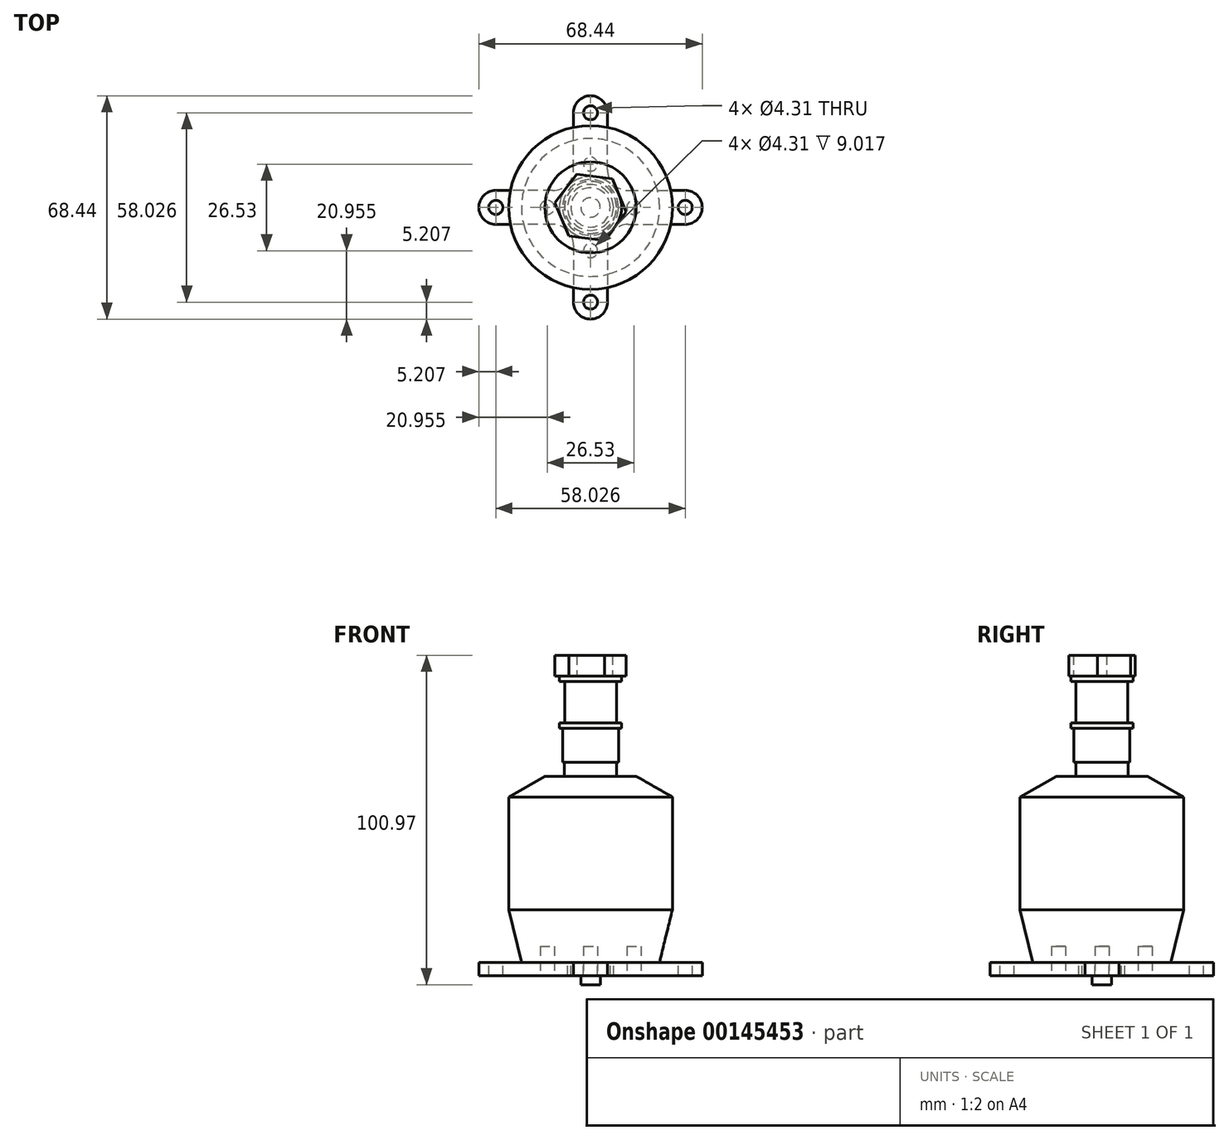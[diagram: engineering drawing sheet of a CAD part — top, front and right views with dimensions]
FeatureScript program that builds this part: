
annotation { "Feature Type Name" : "Feature", "Feature Type Description" : "" }
export const myFeature = defineFeature(function(context is Context, id is Id, definition is map)
    precondition{}
    {
        {
            var Q0;
            Q0=qCreatedBy(makeId("Top.planeOp"),FACE);
            var sketch = newSketch(context, id + "F0", { "sketchPlane" : qUnion([Q0])});
            skCircle(sketch, "E0", {"center": v(0, 0) * mm, "radius": 21.15 * mm});
            skSolve(sketch);
        }
        {
            var Q0;
            Q0=qCreatedBy(makeId("Top.planeOp"),FACE);
            cPlane(context, id + "F1", {"entities" : qUnion([Q0]), "cplaneType" : CPlaneType.OFFSET, "offset" : 16.13 * mm, "width" : 152.4 * mm, "height" : 152.4 * mm});
        }
        {
            var Q0;
            Q0=qCreatedBy(id+"F1.planeOp",FACE);
            var sketch = newSketch(context, id + "F2", { "sketchPlane" : qUnion([Q0])});
            skCircle(sketch, "E1", {"center": v(0, 0) * mm, "radius": 25.08 * mm});
            skSolve(sketch);
        }
        {
            var Q0;
            Q0=makeQuery(id+"F0.imprint","IMPRINT",FACE,{"disambiguationData":[TD([[makeQuery(id+"F0.imprint","IMPRINT",EDGE,{"derivedFrom":sQuery(id+"F0.wireOp",EDGE,"E0")}),1.0]])]});
            var Q1;
            Q1=makeQuery(id+"F2.imprint","IMPRINT",FACE,{"disambiguationData":[TD([[makeQuery(id+"F2.imprint","IMPRINT",EDGE,{"derivedFrom":sQuery(id+"F2.wireOp",EDGE,"E1")}),1.0]])]});
            loft(context, id + "F3", {"sheetProfilesArray" : [{ "sheetProfileEntities" : qUnion([Q0]) }, { "sheetProfileEntities" : qUnion([Q1]) }]});
        }
        {
            var Q0;
            Q0=makeQuery(id+"F3.opLoft","CAP_FACE",FACE,{"disambiguationData":[OSD([makeQuery(id+"F2.imprint","IMPRINT",FACE,{"disambiguationData":[TD([[makeQuery(id+"F2.imprint","IMPRINT",EDGE,{"derivedFrom":sQuery(id+"F2.wireOp",EDGE,"E1")}),1.0]])]})])],"isStart":true});
            extrude(context, id + "F4", {"entities" : qUnion([Q0]), "depth" : 34.54 * mm});
        }
        {
            var Q0;
            Q0=makeQuery(id+"F4.opExtrude","CAP_FACE",FACE,{"disambiguationData":[OSD([makeQuery(id+"F2.imprint","IMPRINT",FACE,{"disambiguationData":[TD([[makeQuery(id+"F2.imprint","IMPRINT",EDGE,{"derivedFrom":sQuery(id+"F2.wireOp",EDGE,"E1")}),1.0]])]})])],"isStart":false});
            cPlane(context, id + "F5", {"entities" : qUnion([Q0]), "cplaneType" : CPlaneType.OFFSET, "offset" : 6.35 * mm, "width" : 152.4 * mm, "height" : 152.4 * mm});
        }
        {
            var Q0;
            Q0=qCreatedBy(id+"F5.planeOp",FACE);
            var sketch = newSketch(context, id + "F6", { "sketchPlane" : qUnion([Q0])});
            skCircle(sketch, "E2", {"center": v(0, 0) * mm, "radius": 13.97 * mm});
            skSolve(sketch);
        }
        {
            var Q1;
            Q1=makeQuery(id+"F6.imprint","IMPRINT",FACE,{"disambiguationData":[TD([[makeQuery(id+"F6.imprint","IMPRINT",EDGE,{"derivedFrom":sQuery(id+"F6.wireOp",EDGE,"E2")}),1.0]])]});
            var Q2;
            Q2=makeQuery(id+"F4.opExtrude","CAP_FACE",FACE,{"disambiguationData":[OSD([makeQuery(id+"F2.imprint","IMPRINT",FACE,{"disambiguationData":[TD([[makeQuery(id+"F2.imprint","IMPRINT",EDGE,{"derivedFrom":sQuery(id+"F2.wireOp",EDGE,"E1")}),1.0]])]})])],"isStart":false});
            loft(context, id + "F7", {"operationType" : NewBodyOperationType.ADD, "sheetProfilesArray" : [{ "sheetProfileEntities" : qUnion([Q1]) }, { "sheetProfileEntities" : qUnion([Q2]) }]});
        }
        {
            var Q0;
            Q0=makeQuery(id+"F7.opLoft","CAP_FACE",FACE,{"disambiguationData":[OSD([makeQuery(id+"F6.imprint","IMPRINT",FACE,{"disambiguationData":[TD([[makeQuery(id+"F6.imprint","IMPRINT",EDGE,{"derivedFrom":sQuery(id+"F6.wireOp",EDGE,"E2")}),1.0]])]})])],"isStart":true});
            var sketch = newSketch(context, id + "F8", { "sketchPlane" : qUnion([Q0])});
            skCircle(sketch, "E3", {"center": v(0, 0) * mm, "radius": 8 * mm});
            skSolve(sketch);
        }
        {
            var Q0;
            Q0 = qSketchRegion(id + "F8", true);
            extrude(context, id + "F9", {"entities" : qUnion([Q0]), "operationType" : NewBodyOperationType.ADD, "depth" : 4.32 * mm});
        }
        {
            var Q0;
            Q0=makeQuery(id+"F9.opExtrude","CAP_FACE",FACE,{"disambiguationData":[OSD([sQuery(id+"F8.wireOp",EDGE,"E3")])],"isStart":false});
            var sketch = newSketch(context, id + "F10", { "sketchPlane" : qUnion([Q0])});
            skCircle(sketch, "E4", {"center": v(0, 0) * mm, "radius": 3 * mm});
            skSolve(sketch);
        }
        {
            var Q0;
            Q0 = qSketchRegion(id + "F10", true);
            extrude(context, id + "F11", {"entities" : qUnion([Q0]), "operationType" : NewBodyOperationType.ADD, "depth" : 15.24 * mm});
        }
        {
            var Q0;
            Q0=makeQuery(id+"F3.opLoft","CAP_FACE",FACE,{"disambiguationData":[OSD([makeQuery(id+"F0.imprint","IMPRINT",FACE,{"disambiguationData":[TD([[makeQuery(id+"F0.imprint","IMPRINT",EDGE,{"derivedFrom":sQuery(id+"F0.wireOp",EDGE,"E0")}),1.0]])]})])],"isStart":true});
            var sketch = newSketch(context, id + "F12", { "sketchPlane" : qUnion([Q0])});
            skCircle(sketch, "E5", {"center": v(0, 0) * mm, "radius": 6.03 * mm});
            skSolve(sketch);
        }
        {
            var Q0;
            Q0 = qSketchRegion(id + "F12", true);
            extrude(context, id + "F13", {"entities" : qUnion([Q0]), "operationType" : NewBodyOperationType.ADD, "depth" : 4.06 * mm});
        }
        {
            var Q0;
            Q0=makeQuery(id+"F13.opExtrude","CAP_FACE",FACE,{"disambiguationData":[OSD([sQuery(id+"F12.wireOp",EDGE,"E5")])],"isStart":false});
            var sketch = newSketch(context, id + "F14", { "sketchPlane" : qUnion([Q0])});
            skCircle(sketch, "E6", {"center": v(0, 0) * mm, "radius": 2.98 * mm});
            skSolve(sketch);
        }
        {
            var Q0;
            Q0 = qSketchRegion(id + "F14", true);
            extrude(context, id + "F15", {"entities" : qUnion([Q0]), "operationType" : NewBodyOperationType.ADD, "depth" : 2.8 * mm});
        }
        {
            var Q0;
            Q0=makeQuery(id+"F3.opLoft","CAP_FACE",FACE,{"disambiguationData":[OSD([makeQuery(id+"F0.imprint","IMPRINT",FACE,{"disambiguationData":[TD([[makeQuery(id+"F0.imprint","IMPRINT",EDGE,{"derivedFrom":sQuery(id+"F0.wireOp",EDGE,"E0")}),1.0]])]})])],"isStart":true});
            var sketch = newSketch(context, id + "F16", { "sketchPlane" : qUnion([Q0])});
            skCircle(sketch, "E7", {"center": v(0, 13.27) * mm, "radius": 2.15 * mm});
            skCircle(sketch, "E8", {"center": v(13.27, 0) * mm, "radius": 2.15 * mm});
            skCircle(sketch, "E9", {"center": v(0, -13.27) * mm, "radius": 2.15 * mm});
            skCircle(sketch, "E10", {"center": v(-13.27, 0) * mm, "radius": 2.15 * mm});
            skCircle(sketch, "E11", {"center": v(0, 0) * mm, "radius": 11.11 * mm, "construction": true});
            skSolve(sketch);
        }
        {
            var Q0;
            Q0 = qSketchRegion(id + "F16", true);
            extrude(context, id + "F17", {"entities" : qUnion([Q0]), "operationType" : NewBodyOperationType.REMOVE, "oppositeDirection" : true, "depth" : 4.95 * mm});
        }
        {
            var Q0;
            Q0=makeQuery(id+"F3.opLoft","CAP_FACE",FACE,{"disambiguationData":[OSD([makeQuery(id+"F0.imprint","IMPRINT",FACE,{"disambiguationData":[TD([[makeQuery(id+"F0.imprint","IMPRINT",EDGE,{"derivedFrom":sQuery(id+"F0.wireOp",EDGE,"E0")}),1.0]])]})])],"isStart":true});
            var sketch = newSketch(context, id + "F18", { "sketchPlane" : qUnion([Q0])});
            skCircle(sketch, "E12", {"center": v(0, 0) * mm, "radius": 7.05 * mm});
            skLineSegment(sketch, "E13.left", {"start": v(5.2, 11.56) * mm, "end": v(5.2, 29.01) * mm});
            skLineSegment(sketch, "E13.right", {"start": v(-5.2, 11.56) * mm, "end": v(-5.2, 29.01) * mm});
            skPoint(sketch, "E13.middle", {"position": v(0, 18.28) * mm});
            skLineSegment(sketch, "E14", {"start": v(-5.2, 29.01) * mm, "end": v(5.2, 29.01) * mm, "construction": true});
            skArc(sketch, "E15", {"start": v(5.2, 29.01) * mm, "mid": v(0, 34.22) * mm, "end": v(-5.2, 29.01) * mm});
            skCircle(sketch, "E16", {"center": v(0, 29.01) * mm, "radius": 2.15 * mm});
            skLineSegment(sketch, "E17.MirrorCS", {"start": v(-5.2, -29.01) * mm, "end": v(5.2, -29.01) * mm, "construction": true});
            skCircle(sketch, "E18.MirrorC", {"center": v(0, -29.01) * mm, "radius": 2.15 * mm});
            skLineSegment(sketch, "E19.MirrorCS", {"start": v(5.2, -11.56) * mm, "end": v(5.2, -29.01) * mm});
            skLineSegment(sketch, "E20.MirrorCS", {"start": v(-5.2, -11.56) * mm, "end": v(-5.2, -29.01) * mm});
            skPoint(sketch, "E21.MirrorP", {"position": v(0, -18.28) * mm});
            skArc(sketch, "E22.MirrorCS", {"start": v(5.2, -29.01) * mm, "mid": v(0, -34.22) * mm, "end": v(-5.2, -29.01) * mm});
            skLineSegment(sketch, "E23.bottom", {"start": v(-11.56, 5.2) * mm, "end": v(-29.01, 5.2) * mm});
            skLineSegment(sketch, "E23.top", {"start": v(-11.56, -5.2) * mm, "end": v(-29.01, -5.2) * mm});
            skPoint(sketch, "E23.middle", {"position": v(-18.28, 0) * mm});
            skLineSegment(sketch, "E24", {"start": v(-29.01, 5.2) * mm, "end": v(-29.01, -5.2) * mm, "construction": true});
            skCircle(sketch, "E25", {"center": v(-29.01, 0) * mm, "radius": 2.15 * mm});
            skArc(sketch, "E26", {"start": v(-29.01, 5.2) * mm, "mid": v(-34.22, 0) * mm, "end": v(-29.01, -5.2) * mm});
            skLineSegment(sketch, "E27.MirrorCS", {"start": v(11.56, -5.2) * mm, "end": v(29.01, -5.2) * mm});
            skCircle(sketch, "E28.MirrorC", {"center": v(29.01, 0) * mm, "radius": 2.15 * mm});
            skPoint(sketch, "E29.MirrorP", {"position": v(18.28, 0) * mm});
            skArc(sketch, "E30.MirrorCS", {"start": v(29.01, 5.2) * mm, "mid": v(34.22, 0) * mm, "end": v(29.01, -5.2) * mm});
            skLineSegment(sketch, "E31.MirrorCS", {"start": v(29.01, 5.2) * mm, "end": v(29.01, -5.2) * mm, "construction": true});
            skLineSegment(sketch, "E32.MirrorCS", {"start": v(11.56, 5.2) * mm, "end": v(29.01, 5.2) * mm});
            skArc(sketch, "E33.filletArc", {"start": v(-11.56, 5.2) * mm, "mid": v(-7.07, 7.07) * mm, "end": v(-5.2, 11.56) * mm});
            skArc(sketch, "E34.filletArc", {"start": v(-5.2, -11.56) * mm, "mid": v(-7.07, -7.07) * mm, "end": v(-11.56, -5.2) * mm});
            skArc(sketch, "E35.filletArc", {"start": v(11.56, -5.2) * mm, "mid": v(7.07, -7.07) * mm, "end": v(5.2, -11.56) * mm});
            skArc(sketch, "E36.filletArc", {"start": v(5.2, 11.56) * mm, "mid": v(7.07, 7.07) * mm, "end": v(11.56, 5.2) * mm});
            skPoint(sketch, "E37.orphan", {"position": v(-34.99, 5.2) * mm});
            skPoint(sketch, "E38.orphan", {"position": v(-31.03, -5.2) * mm});
            skPoint(sketch, "E39.orphan", {"position": v(-5.2, -34.22) * mm});
            skPoint(sketch, "E40.orphan", {"position": v(5.2, -34.22) * mm});
            skPoint(sketch, "E41.orphan", {"position": v(31.03, -5.2) * mm});
            skPoint(sketch, "E42.MirrorCS.start.orphan", {"position": v(34.99, 5.2) * mm});
            skPoint(sketch, "E43.orphan", {"position": v(5.2, 34.22) * mm});
            skPoint(sketch, "E44.orphan", {"position": v(-5.2, 34.22) * mm});
            skCircle(sketch, "E45", {"center": v(-13.27, 0) * mm, "radius": 2.15 * mm});
            skCircle(sketch, "E46", {"center": v(0, 13.27) * mm, "radius": 2.15 * mm});
            skCircle(sketch, "E47", {"center": v(13.27, 0) * mm, "radius": 2.15 * mm});
            skCircle(sketch, "E48", {"center": v(0, -13.27) * mm, "radius": 2.15 * mm});
            skSolve(sketch);
        }
        {
            var Q0;
            Q0 = qSketchRegion(id + "F18", true);
            extrude(context, id + "F19", {"entities" : qUnion([Q0]), "operationType" : NewBodyOperationType.ADD, "depth" : 4.06 * mm});
        }
        {
            var Q0;
            Q0=makeQuery(id+"F9.opExtrude","CAP_FACE",FACE,{"disambiguationData":[OSD([sQuery(id+"F8.wireOp",EDGE,"E3")])],"isStart":false});
            var sketch = newSketch(context, id + "F20", { "sketchPlane" : qUnion([Q0])});
            skCircle(sketch, "E49", {"center": v(0, 0) * mm, "radius": 8.57 * mm});
            skSolve(sketch);
        }
        {
            var Q0;
            Q0 = qSketchRegion(id + "F20", true);
            extrude(context, id + "F21", {"entities" : qUnion([Q0]), "operationType" : NewBodyOperationType.ADD, "depth" : 10.4 * mm});
        }
        {
            var Q0;
            Q0=makeQuery(id+"F21.opExtrude","CAP_FACE",FACE,{"disambiguationData":[OSD([sQuery(id+"F20.wireOp",EDGE,"E49")])],"isStart":false});
            var sketch = newSketch(context, id + "F22", { "sketchPlane" : qUnion([Q0])});
            skCircle(sketch, "E50", {"center": v(0, 0) * mm, "radius": 9.53 * mm});
            skSolve(sketch);
        }
        {
            var Q0;
            Q0 = qSketchRegion(id + "F22", true);
            extrude(context, id + "F23", {"entities" : qUnion([Q0]), "operationType" : NewBodyOperationType.ADD, "depth" : 1.65 * mm});
        }
        {
            var Q0;
            Q0=makeQuery(id+"F23.opExtrude","CAP_FACE",FACE,{"disambiguationData":[OSD([sQuery(id+"F22.wireOp",EDGE,"E50")])],"isStart":false});
            var sketch = newSketch(context, id + "F24", { "sketchPlane" : qUnion([Q0])});
            skCircle(sketch, "E51", {"center": v(0, 0) * mm, "radius": 7.94 * mm});
            skSolve(sketch);
        }
        {
            var Q0;
            Q0 = qSketchRegion(id + "F24", true);
            extrude(context, id + "F25", {"entities" : qUnion([Q0]), "operationType" : NewBodyOperationType.ADD, "depth" : 12.7 * mm});
        }
        {
            var Q0;
            Q0=makeQuery(id+"F25.opExtrude","CAP_FACE",FACE,{"disambiguationData":[OSD([sQuery(id+"F24.wireOp",EDGE,"E51")])],"isStart":false});
            var sketch = newSketch(context, id + "F26", { "sketchPlane" : qUnion([Q0])});
            skCircle(sketch, "E52", {"center": v(0, 0) * mm, "radius": 9.53 * mm});
            skSolve(sketch);
        }
        {
            var Q0;
            Q0 = qSketchRegion(id + "F26", true);
            var Q1;
            Q1=makeQuery(id+"F26.imprint","IMPRINT",FACE,{"disambiguationData":[TD([[makeQuery(id+"F26.imprint","IMPRINT",EDGE,{"derivedFrom":sQuery(id+"F26.wireOp",EDGE,"3Mybu0Wv-YXiH-vT5i-18px-TGbjftWIMi0C")}),1.0]])]});
            extrude(context, id + "F27", {"entities" : qUnion([Q0, Q1]), "operationType" : NewBodyOperationType.ADD, "depth" : 1.65 * mm});
        }
        {
            var Q0;
            Q0=makeQuery(id+"F27.opExtrude","CAP_FACE",FACE,{"disambiguationData":[OSD([sQuery(id+"F26.wireOp",EDGE,"E52")])],"isStart":false});
            var sketch = newSketch(context, id + "F28", { "sketchPlane" : qUnion([Q0])});
            skCircle(sketch, "E53.cCircle", {"center": v(0, 0) * mm, "radius": 9.53 * mm, "construction": true});
            skLineSegment(sketch, "E53.0", {"start": v(-4.26, 10.14) * mm, "end": v(6.65, 8.76) * mm});
            skLineSegment(sketch, "E53.1", {"start": v(6.65, 8.76) * mm, "end": v(10.91, -1.38) * mm});
            skLineSegment(sketch, "E53.2", {"start": v(10.91, -1.38) * mm, "end": v(4.26, -10.14) * mm});
            skLineSegment(sketch, "E53.3", {"start": v(4.26, -10.14) * mm, "end": v(-6.65, -8.76) * mm});
            skLineSegment(sketch, "E53.4", {"start": v(-6.65, -8.76) * mm, "end": v(-10.91, 1.38) * mm});
            skLineSegment(sketch, "E53.5", {"start": v(-10.91, 1.38) * mm, "end": v(-4.26, 10.14) * mm});
            skPoint(sketch, "E53.0.midPoint", {"position": v(1.2, 9.45) * mm});
            skSolve(sketch);
        }
        {
            var Q0;
            Q0 = qSketchRegion(id + "F28", true);
            extrude(context, id + "F29", {"entities" : qUnion([Q0]), "operationType" : NewBodyOperationType.ADD, "depth" : 6.35 * mm});
        }
    });
